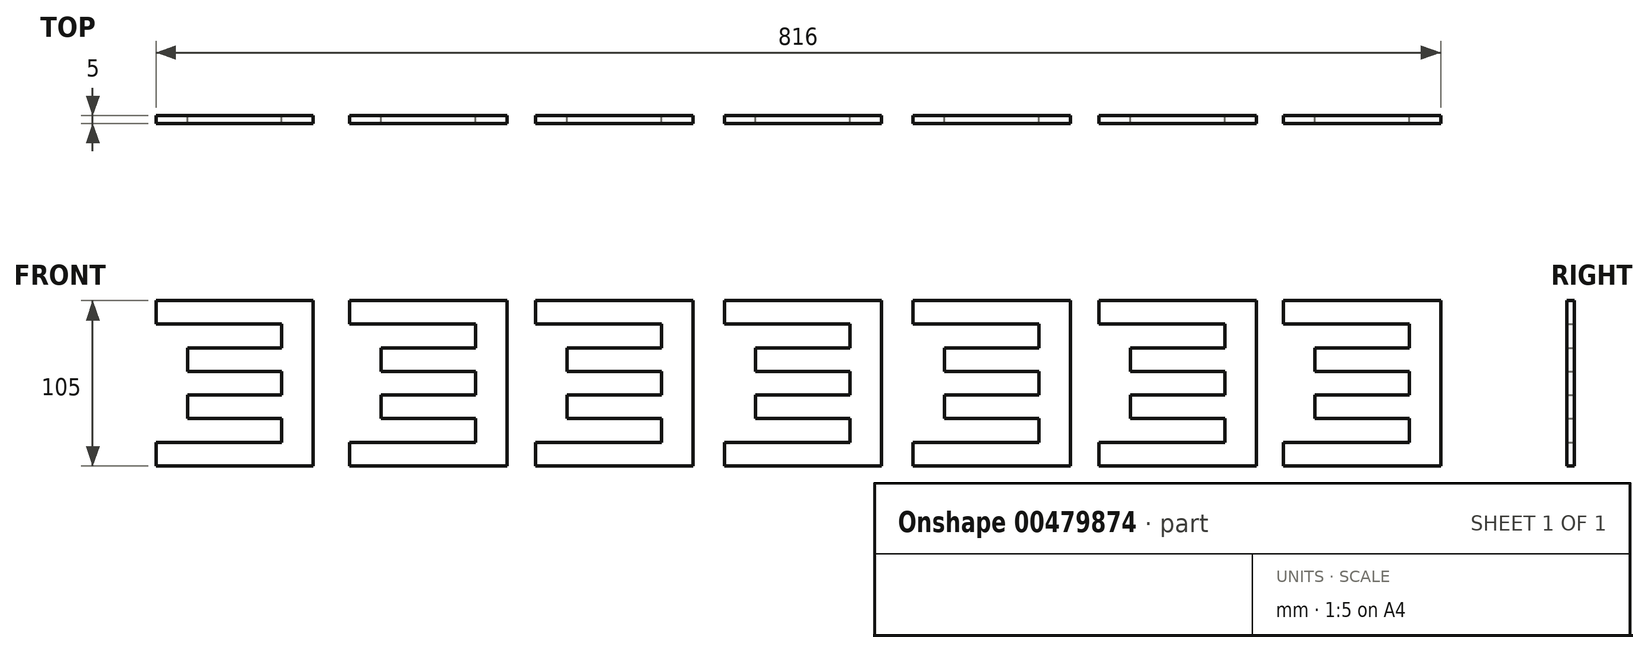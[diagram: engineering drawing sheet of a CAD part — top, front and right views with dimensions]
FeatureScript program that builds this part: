
annotation { "Feature Type Name" : "Feature", "Feature Type Description" : "" }
export const myFeature = defineFeature(function(context is Context, id is Id, definition is map)
    precondition{}
    {
        {
            var Q0;
            Q0=qCreatedBy(makeId("Front.planeOp"),FACE);
            var sketch = newSketch(context, id + "F0", { "sketchPlane" : qUnion([Q0])});
            skLineSegment(sketch, "E0.bottom", {"start": v(-40.92, 38.18) * mm, "end": v(39.08, 38.18) * mm});
            skLineSegment(sketch, "E0.top", {"start": v(-40.92, -36.82) * mm, "end": v(39.08, -36.82) * mm});
            skLineSegment(sketch, "E0.right", {"start": v(39.08, 38.18) * mm, "end": v(39.08, 23.18) * mm});
            skLineSegment(sketch, "E1", {"start": v(-20.92, 23.18) * mm, "end": v(-20.92, 8.18) * mm});
            skLineSegment(sketch, "E2", {"start": v(-20.92, 23.18) * mm, "end": v(39.08, 23.18) * mm});
            skLineSegment(sketch, "E3", {"start": v(-20.92, 8.18) * mm, "end": v(39.08, 8.18) * mm});
            skLineSegment(sketch, "E4", {"start": v(-20.92, -6.82) * mm, "end": v(39.08, -6.82) * mm});
            skLineSegment(sketch, "E5", {"start": v(-20.92, -21.82) * mm, "end": v(39.08, -21.82) * mm});
            skLineSegment(sketch, "E6.trimOffspring", {"start": v(-20.92, -6.82) * mm, "end": v(-20.92, -21.82) * mm});
            skLineSegment(sketch, "E7.trimOffspring", {"start": v(39.08, 8.18) * mm, "end": v(39.08, -6.82) * mm});
            skLineSegment(sketch, "E8.trimOffspring", {"start": v(39.08, -21.82) * mm, "end": v(39.08, -36.82) * mm});
            skLineSegment(sketch, "E9", {"start": v(-40.92, 38.18) * mm, "end": v(-40.92, 53.18) * mm});
            skLineSegment(sketch, "E10", {"start": v(-40.92, 53.18) * mm, "end": v(59.08, 53.18) * mm});
            skLineSegment(sketch, "E11", {"start": v(59.08, 53.18) * mm, "end": v(59.08, -51.82) * mm});
            skLineSegment(sketch, "E12", {"start": v(59.08, -51.82) * mm, "end": v(-40.92, -51.82) * mm});
            skLineSegment(sketch, "E13", {"start": v(-40.92, -51.82) * mm, "end": v(-40.92, -36.82) * mm});
            skSolve(sketch);
        }
        {
            var Q0;
            Q0 = qSketchRegion(id + "F0", true);
            extrude(context, id + "F1", {"entities" : qUnion([Q0]), "depth" : 5 * mm});
        }
        {
            var Q0;
            Q0=qCreatedBy(makeId("Right.planeOp"),FACE);
            var sketch = newSketch(context, id + "F2", { "sketchPlane" : qUnion([Q0])});
            skLineSegment(sketch, "E14.bottom", {"start": v(-47.5, 37.5) * mm, "end": v(32.5, 37.5) * mm});
            skLineSegment(sketch, "E14.top", {"start": v(-47.5, -37.5) * mm, "end": v(32.5, -37.5) * mm});
            skLineSegment(sketch, "E14.right", {"start": v(32.5, 37.5) * mm, "end": v(32.5, 22.5) * mm});
            skLineSegment(sketch, "E15", {"start": v(-27.5, 22.5) * mm, "end": v(-27.5, 7.5) * mm});
            skLineSegment(sketch, "E16", {"start": v(-27.5, 22.5) * mm, "end": v(32.5, 22.5) * mm});
            skLineSegment(sketch, "E17", {"start": v(-27.5, 7.5) * mm, "end": v(32.5, 7.5) * mm});
            skLineSegment(sketch, "E18", {"start": v(-27.5, -7.5) * mm, "end": v(32.5, -7.5) * mm});
            skLineSegment(sketch, "E19", {"start": v(-27.5, -22.5) * mm, "end": v(32.5, -22.5) * mm});
            skLineSegment(sketch, "E20.trimOffspring", {"start": v(-27.5, -7.5) * mm, "end": v(-27.5, -22.5) * mm});
            skLineSegment(sketch, "E21.trimOffspring", {"start": v(32.5, 7.5) * mm, "end": v(32.5, -7.5) * mm});
            skLineSegment(sketch, "E22.trimOffspring", {"start": v(32.5, -22.5) * mm, "end": v(32.5, -37.5) * mm});
            skLineSegment(sketch, "E23", {"start": v(-47.5, 37.5) * mm, "end": v(-47.5, 52.5) * mm});
            skLineSegment(sketch, "E24", {"start": v(-47.5, 52.5) * mm, "end": v(52.5, 52.5) * mm});
            skLineSegment(sketch, "E25", {"start": v(52.5, 52.5) * mm, "end": v(52.5, -52.5) * mm});
            skLineSegment(sketch, "E26", {"start": v(52.5, -52.5) * mm, "end": v(-47.5, -52.5) * mm});
            skLineSegment(sketch, "E27", {"start": v(-47.5, -52.5) * mm, "end": v(-47.5, -37.5) * mm});
            skSolve(sketch);
        }
        {
            var Q0;
            Q0=makeQuery(id+"F2.imprint","IMPRINT",FACE,{"disambiguationData":[TD([[makeQuery(id+"F2.imprint","IMPRINT",EDGE,{"derivedFrom":sQuery(id+"F2.wireOp",EDGE,"E14.bottom")}),1.0]])]});
            extrude(context, id + "F3", {"entities" : qUnion([Q0]), "depth" : 5 * mm});
        }
        {
            var Q0;
            Q0=makeQuery(id+"F1.opExtrude","SWEPT_BODY",BODY,{"disambiguationData":[OSD([sQuery(id+"F0.wireOp",EDGE,"E0.bottom"),sQuery(id+"F0.wireOp",EDGE,"E0.top"),sQuery(id+"F0.wireOp",EDGE,"E0.right"),sQuery(id+"F0.wireOp",EDGE,"E1"),sQuery(id+"F0.wireOp",EDGE,"E2"),sQuery(id+"F0.wireOp",EDGE,"E3"),sQuery(id+"F0.wireOp",EDGE,"E4"),sQuery(id+"F0.wireOp",EDGE,"E5"),sQuery(id+"F0.wireOp",EDGE,"E6.trimOffspring"),sQuery(id+"F0.wireOp",EDGE,"E7.trimOffspring"),sQuery(id+"F0.wireOp",EDGE,"E8.trimOffspring"),sQuery(id+"F0.wireOp",EDGE,"E9"),sQuery(id+"F0.wireOp",EDGE,"E10"),sQuery(id+"F0.wireOp",EDGE,"E11"),sQuery(id+"F0.wireOp",EDGE,"E12"),sQuery(id+"F0.wireOp",EDGE,"E13")])]});
            var Q1;
            Q1=makeQuery(id+"F3.opExtrude","SWEPT_BODY",BODY,{"disambiguationData":[OSD([sQuery(id+"F2.wireOp",EDGE,"E14.bottom"),sQuery(id+"F2.wireOp",EDGE,"E14.top"),sQuery(id+"F2.wireOp",EDGE,"E14.right"),sQuery(id+"F2.wireOp",EDGE,"E15"),sQuery(id+"F2.wireOp",EDGE,"E16"),sQuery(id+"F2.wireOp",EDGE,"E17"),sQuery(id+"F2.wireOp",EDGE,"E18"),sQuery(id+"F2.wireOp",EDGE,"E19"),sQuery(id+"F2.wireOp",EDGE,"E20.trimOffspring"),sQuery(id+"F2.wireOp",EDGE,"E21.trimOffspring"),sQuery(id+"F2.wireOp",EDGE,"E22.trimOffspring"),sQuery(id+"F2.wireOp",EDGE,"E23"),sQuery(id+"F2.wireOp",EDGE,"E24"),sQuery(id+"F2.wireOp",EDGE,"E25"),sQuery(id+"F2.wireOp",EDGE,"E26"),sQuery(id+"F2.wireOp",EDGE,"E27")])]});
            transform(context, id + "F4", {"entities" : qUnion([Q0, Q1]), "transformType" : TransformType.TRANSLATION_3D, "dx" : 120 * mm, "dy" : 0 * mm, "dz" : 0 * mm, "makeCopy" : true});
        }
        {
            var Q0;
            Q0=makeQuery(id+"F1.opExtrude","SWEPT_BODY",BODY,{"disambiguationData":[OSD([sQuery(id+"F0.wireOp",EDGE,"E0.bottom"),sQuery(id+"F0.wireOp",EDGE,"E0.top"),sQuery(id+"F0.wireOp",EDGE,"E0.right"),sQuery(id+"F0.wireOp",EDGE,"E1"),sQuery(id+"F0.wireOp",EDGE,"E2"),sQuery(id+"F0.wireOp",EDGE,"E3"),sQuery(id+"F0.wireOp",EDGE,"E4"),sQuery(id+"F0.wireOp",EDGE,"E5"),sQuery(id+"F0.wireOp",EDGE,"E6.trimOffspring"),sQuery(id+"F0.wireOp",EDGE,"E7.trimOffspring"),sQuery(id+"F0.wireOp",EDGE,"E8.trimOffspring"),sQuery(id+"F0.wireOp",EDGE,"E9"),sQuery(id+"F0.wireOp",EDGE,"E10"),sQuery(id+"F0.wireOp",EDGE,"E11"),sQuery(id+"F0.wireOp",EDGE,"E12"),sQuery(id+"F0.wireOp",EDGE,"E13")])]});
            transform(context, id + "F5", {"entities" : qUnion([Q0]), "transformType" : TransformType.TRANSLATION_3D, "dx" : 240 * mm, "dy" : 0 * mm, "dz" : 0 * mm, "makeCopy" : true});
        }
        {
            var Q0;
            Q0=makeQuery(id+"F3.opExtrude","SWEPT_BODY",BODY,{"disambiguationData":[OSD([sQuery(id+"F2.wireOp",EDGE,"E14.bottom"),sQuery(id+"F2.wireOp",EDGE,"E14.top"),sQuery(id+"F2.wireOp",EDGE,"E14.right"),sQuery(id+"F2.wireOp",EDGE,"E15"),sQuery(id+"F2.wireOp",EDGE,"E16"),sQuery(id+"F2.wireOp",EDGE,"E17"),sQuery(id+"F2.wireOp",EDGE,"E18"),sQuery(id+"F2.wireOp",EDGE,"E19"),sQuery(id+"F2.wireOp",EDGE,"E20.trimOffspring"),sQuery(id+"F2.wireOp",EDGE,"E21.trimOffspring"),sQuery(id+"F2.wireOp",EDGE,"E22.trimOffspring"),sQuery(id+"F2.wireOp",EDGE,"E23"),sQuery(id+"F2.wireOp",EDGE,"E24"),sQuery(id+"F2.wireOp",EDGE,"E25"),sQuery(id+"F2.wireOp",EDGE,"E26"),sQuery(id+"F2.wireOp",EDGE,"E27")])]});
            deleteBodies(context, id + "F6", {"entities" : qUnion([Q0])});
        }
        {
            var Q0;
            Q0=makeQuery(id+"F4.opPattern","COPY",BODY,{"derivedFrom":makeQuery(id+"F3.opExtrude","SWEPT_BODY",BODY,{"disambiguationData":[OSD([sQuery(id+"F2.wireOp",EDGE,"E14.bottom"),sQuery(id+"F2.wireOp",EDGE,"E14.top"),sQuery(id+"F2.wireOp",EDGE,"E14.right"),sQuery(id+"F2.wireOp",EDGE,"E15"),sQuery(id+"F2.wireOp",EDGE,"E16"),sQuery(id+"F2.wireOp",EDGE,"E17"),sQuery(id+"F2.wireOp",EDGE,"E18"),sQuery(id+"F2.wireOp",EDGE,"E19"),sQuery(id+"F2.wireOp",EDGE,"E20.trimOffspring"),sQuery(id+"F2.wireOp",EDGE,"E21.trimOffspring"),sQuery(id+"F2.wireOp",EDGE,"E22.trimOffspring"),sQuery(id+"F2.wireOp",EDGE,"E23"),sQuery(id+"F2.wireOp",EDGE,"E24"),sQuery(id+"F2.wireOp",EDGE,"E25"),sQuery(id+"F2.wireOp",EDGE,"E26"),sQuery(id+"F2.wireOp",EDGE,"E27")])]}),"instanceName":"1"});
            deleteBodies(context, id + "F7", {"entities" : qUnion([Q0])});
        }
        {
            var Q0;
            Q0=makeQuery(id+"F5.opPattern","COPY",BODY,{"derivedFrom":makeQuery(id+"F1.opExtrude","SWEPT_BODY",BODY,{"disambiguationData":[OSD([sQuery(id+"F0.wireOp",EDGE,"E0.bottom"),sQuery(id+"F0.wireOp",EDGE,"E0.top"),sQuery(id+"F0.wireOp",EDGE,"E0.right"),sQuery(id+"F0.wireOp",EDGE,"E1"),sQuery(id+"F0.wireOp",EDGE,"E2"),sQuery(id+"F0.wireOp",EDGE,"E3"),sQuery(id+"F0.wireOp",EDGE,"E4"),sQuery(id+"F0.wireOp",EDGE,"E5"),sQuery(id+"F0.wireOp",EDGE,"E6.trimOffspring"),sQuery(id+"F0.wireOp",EDGE,"E7.trimOffspring"),sQuery(id+"F0.wireOp",EDGE,"E8.trimOffspring"),sQuery(id+"F0.wireOp",EDGE,"E9"),sQuery(id+"F0.wireOp",EDGE,"E10"),sQuery(id+"F0.wireOp",EDGE,"E11"),sQuery(id+"F0.wireOp",EDGE,"E12"),sQuery(id+"F0.wireOp",EDGE,"E13")])]}),"instanceName":"1"});
            transform(context, id + "F8", {"entities" : qUnion([Q0]), "transformType" : TransformType.TRANSLATION_3D, "dx" : 118 * mm, "dy" : 0 * mm, "dz" : 0 * mm, "makeCopy" : true});
        }
        {
            var Q0;
            Q0=makeQuery(id+"F8.opPattern","COPY",BODY,{"derivedFrom":makeQuery(id+"F5.opPattern","COPY",BODY,{"derivedFrom":makeQuery(id+"F1.opExtrude","SWEPT_BODY",BODY,{"disambiguationData":[OSD([sQuery(id+"F0.wireOp",EDGE,"E0.bottom"),sQuery(id+"F0.wireOp",EDGE,"E0.top"),sQuery(id+"F0.wireOp",EDGE,"E0.right"),sQuery(id+"F0.wireOp",EDGE,"E1"),sQuery(id+"F0.wireOp",EDGE,"E2"),sQuery(id+"F0.wireOp",EDGE,"E3"),sQuery(id+"F0.wireOp",EDGE,"E4"),sQuery(id+"F0.wireOp",EDGE,"E5"),sQuery(id+"F0.wireOp",EDGE,"E6.trimOffspring"),sQuery(id+"F0.wireOp",EDGE,"E7.trimOffspring"),sQuery(id+"F0.wireOp",EDGE,"E8.trimOffspring"),sQuery(id+"F0.wireOp",EDGE,"E9"),sQuery(id+"F0.wireOp",EDGE,"E10"),sQuery(id+"F0.wireOp",EDGE,"E11"),sQuery(id+"F0.wireOp",EDGE,"E12"),sQuery(id+"F0.wireOp",EDGE,"E13")])]}),"instanceName":"1"}),"instanceName":"1"});
            transform(context, id + "F9", {"entities" : qUnion([Q0]), "transformType" : TransformType.TRANSLATION_3D, "dx" : 117 * mm, "dy" : 0 * mm, "dz" : 0 * mm, "makeCopy" : true});
        }
        {
            var Q0;
            Q0=makeQuery(id+"F1.opExtrude","SWEPT_BODY",BODY,{"disambiguationData":[OSD([sQuery(id+"F0.wireOp",EDGE,"E0.bottom"),sQuery(id+"F0.wireOp",EDGE,"E0.top"),sQuery(id+"F0.wireOp",EDGE,"E0.right"),sQuery(id+"F0.wireOp",EDGE,"E1"),sQuery(id+"F0.wireOp",EDGE,"E2"),sQuery(id+"F0.wireOp",EDGE,"E3"),sQuery(id+"F0.wireOp",EDGE,"E4"),sQuery(id+"F0.wireOp",EDGE,"E5"),sQuery(id+"F0.wireOp",EDGE,"E6.trimOffspring"),sQuery(id+"F0.wireOp",EDGE,"E7.trimOffspring"),sQuery(id+"F0.wireOp",EDGE,"E8.trimOffspring"),sQuery(id+"F0.wireOp",EDGE,"E9"),sQuery(id+"F0.wireOp",EDGE,"E10"),sQuery(id+"F0.wireOp",EDGE,"E11"),sQuery(id+"F0.wireOp",EDGE,"E12"),sQuery(id+"F0.wireOp",EDGE,"E13")])]});
            transform(context, id + "F10", {"entities" : qUnion([Q0]), "transformType" : TransformType.TRANSLATION_3D, "dx" : -118 * mm, "dy" : 0 * mm, "dz" : 0 * mm, "makeCopy" : true});
        }
        {
            var Q0;
            Q0=makeQuery(id+"F10.opPattern","COPY",BODY,{"derivedFrom":makeQuery(id+"F1.opExtrude","SWEPT_BODY",BODY,{"disambiguationData":[OSD([sQuery(id+"F0.wireOp",EDGE,"E0.bottom"),sQuery(id+"F0.wireOp",EDGE,"E0.top"),sQuery(id+"F0.wireOp",EDGE,"E0.right"),sQuery(id+"F0.wireOp",EDGE,"E1"),sQuery(id+"F0.wireOp",EDGE,"E2"),sQuery(id+"F0.wireOp",EDGE,"E3"),sQuery(id+"F0.wireOp",EDGE,"E4"),sQuery(id+"F0.wireOp",EDGE,"E5"),sQuery(id+"F0.wireOp",EDGE,"E6.trimOffspring"),sQuery(id+"F0.wireOp",EDGE,"E7.trimOffspring"),sQuery(id+"F0.wireOp",EDGE,"E8.trimOffspring"),sQuery(id+"F0.wireOp",EDGE,"E9"),sQuery(id+"F0.wireOp",EDGE,"E10"),sQuery(id+"F0.wireOp",EDGE,"E11"),sQuery(id+"F0.wireOp",EDGE,"E12"),sQuery(id+"F0.wireOp",EDGE,"E13")])]}),"instanceName":"1"});
            transform(context, id + "F11", {"entities" : qUnion([Q0]), "transformType" : TransformType.TRANSLATION_3D, "dx" : -123 * mm, "dy" : 0 * mm, "dz" : 0 * mm, "makeCopy" : true});
        }
    });
